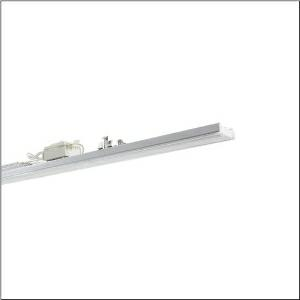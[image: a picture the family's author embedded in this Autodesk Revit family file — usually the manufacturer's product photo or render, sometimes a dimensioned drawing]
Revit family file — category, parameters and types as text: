
# Revit family: licross_11_recessed_mo_51te12dv475g
name_source: partatom
category: Lighting Fixtures
units: mm (PartAtom-declared; Revit-internal decimal feet)

## family parameters
Cut with Voids When Loaded = No
Host = Face
Light Source = No
Part Type = Normal
Room Calculation Point = No
Round Connector Dimension = Use Diameter
Shared = No

## types (1)
- --- (1 x LED, 7640 lm, 40.1 W, 4000K)
    Apparent Load = 40 VA
    CIE Flux Codes = 67 92 99 100 100
    Color Rendering = 80
    Color Temperature = 4000K
    Default Elevation = 1800 mm
    Description = Licross 11 Recessed MO, luminaire insert, of sheet steel, galvanised, coil coated, white, length: 2.250mm, width: 66mm, height: 67mm, LED rated luminous flux: 7.640lm, light colour: 840, SDCM (Standard Deviation of Colour Matching)MacAdam ≤ 2 SDCM (initial), control gear: DALI 2, with plug, 5-pole, with phase selection, mains connection: 220..240V, AC, 50/60Hz, rated input power: 40W, internal wiring halogen-free, primary optical cover: cover, of PMMA, light emission: direct distribution, primary light characteristic: symmetric, protection rating (complete): IP54, insulation class (complete): insulation class I (protective earthing), certification: CE, ENEC, VDE, UKCA, protection symbol: D if used in an environment with non-conductive dust loads with corresponding accessories, impact resistance: IK06, permissible ambient temperature for indoor applications: -25..+45°C, corresponds to IFS (International Featured Standards) requirements for safety and quality in the food industry, reducing of maximum allowable ambient temperature of 5°C with ceiling mounting, LABS conformity tested according to VDMA 24364:2018-05, The light source and the operating device comply with the requirements of the Ecodesign Regulation (EU) 2019/2020 and are replaceable in accordance with this regulation, packaging unit: 1 piece
    Height = 58 mm
    Lamp = 1 x LED
    Lamp Light Flux = 7640 lm
    Lamp Power = 40.1 W
    Lamp count = 1
    Length = 2250 mm
    Luminous efficacy = 191 lm/W
    Manufacturer = Siteco
    ModVariant = No
    Model = 51TE12DV475G
    Mounting Place = Ceiling
    Mounting Type = Pendant
    Number of Poles = 1
    OnlyDefault = Yes
    Power Factor = 1
    Product Name = Licross 11 Recessed MO
    Product group = luminaire insert | ceiling pendant
    ProductGroupID = 901
    Protection Class = Protection class I
    Protection Degree = IP 54
    RLX_Detail_Level = 1
    RLX_Emergency_Light_Flux = 0 lm
    RLX_Emergency_Type = 0
    RLX_Emergency_Type_DB = No
    RlxData = <blob elided: 29269 chars, md5=96e9f8ca>
    Socket = socket
    Standby Power = 0 W
    System Light Flux = 7640 lm
    System Power = 40 W
    Type Comments = factory setting: luminous flux: 100 % | dim-lin: 254 | 180 mA
    Type Image = l_1296930.jpg
    URL = http://relux.com
    VarID = @adj_101771
    Voltage = 0 V
    Weight = 0.00 kg
    Width = 66 mm

## geometry (parser evidence)
native form markers: Blend x4, Sweep x9
no freeform markers — native parametric forms only
